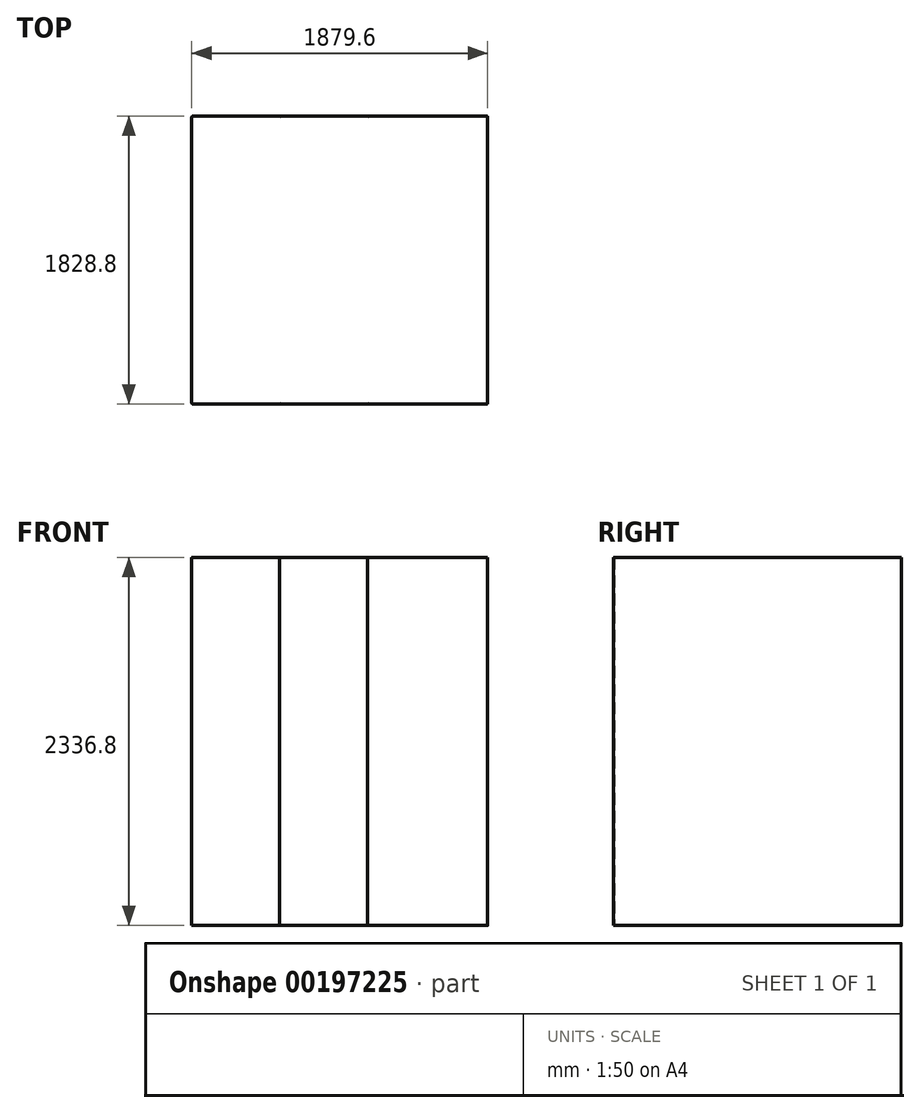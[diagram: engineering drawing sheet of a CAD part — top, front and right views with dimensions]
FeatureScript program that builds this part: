
annotation { "Feature Type Name" : "Feature", "Feature Type Description" : "" }
export const myFeature = defineFeature(function(context is Context, id is Id, definition is map)
    precondition{}
    {
        {
            var Q0;
            Q0=qCreatedBy(makeId("Top.planeOp"),FACE);
            var sketch = newSketch(context, id + "F0", { "sketchPlane" : qUnion([Q0])});
            skLineSegment(sketch, "E0.bottom", {"start": v(-285.75, 914.4) * mm, "end": v(-831.85, 914.4) * mm});
            skLineSegment(sketch, "E0.top", {"start": v(-285.75, -914.4) * mm, "end": v(-831.85, -914.4) * mm});
            skLineSegment(sketch, "E0.left", {"start": v(-279.4, 908.05) * mm, "end": v(-279.4, -908.05) * mm});
            skLineSegment(sketch, "E0.right", {"start": v(-838.2, 908.05) * mm, "end": v(-838.2, -908.05) * mm});
            skPoint(sketch, "E0.middle", {"position": v(-558.8, 0) * mm});
            skLineSegment(sketch, "E1.bottom", {"start": v(273.05, 914.4) * mm, "end": v(-273.05, 914.4) * mm});
            skLineSegment(sketch, "E1.top", {"start": v(273.05, -914.4) * mm, "end": v(-273.05, -914.4) * mm});
            skLineSegment(sketch, "E1.left", {"start": v(279.4, 908.05) * mm, "end": v(279.4, -908.05) * mm});
            skPoint(sketch, "E1.middle", {"position": v(0, 0) * mm});
            skLineSegment(sketch, "E2.bottom", {"start": v(1035.05, 914.4) * mm, "end": v(285.75, 914.4) * mm});
            skLineSegment(sketch, "E2.top", {"start": v(1035.05, -914.4) * mm, "end": v(285.75, -914.4) * mm});
            skLineSegment(sketch, "E2.left", {"start": v(1041.4, 908.05) * mm, "end": v(1041.4, -908.05) * mm});
            skPoint(sketch, "E2.middle", {"position": v(660.4, 0) * mm});
            skPoint(sketch, "E3.visualSharp", {"position": v(279.4, -914.4) * mm});
            skArc(sketch, "E3.filletArc", {"start": v(279.4, -908.05) * mm, "mid": v(281.26, -912.54) * mm, "end": v(285.75, -914.4) * mm});
            skArc(sketch, "E4.filletArc", {"start": v(273.05, -914.4) * mm, "mid": v(277.54, -912.54) * mm, "end": v(279.4, -908.05) * mm});
            skPoint(sketch, "E5.visualSharp", {"position": v(1041.4, -914.4) * mm});
            skArc(sketch, "E5.filletArc", {"start": v(1035.05, -914.4) * mm, "mid": v(1039.54, -912.54) * mm, "end": v(1041.4, -908.05) * mm});
            skPoint(sketch, "E6.visualSharp", {"position": v(1041.4, 914.4) * mm});
            skArc(sketch, "E6.filletArc", {"start": v(1041.4, 908.05) * mm, "mid": v(1039.54, 912.54) * mm, "end": v(1035.05, 914.4) * mm});
            skPoint(sketch, "E7.visualSharp", {"position": v(279.4, 914.4) * mm});
            skArc(sketch, "E7.filletArc", {"start": v(285.75, 914.4) * mm, "mid": v(281.26, 912.54) * mm, "end": v(279.4, 908.05) * mm});
            skArc(sketch, "E8.filletArc", {"start": v(279.4, 908.05) * mm, "mid": v(277.54, 912.54) * mm, "end": v(273.05, 914.4) * mm});
            skPoint(sketch, "E9.visualSharp", {"position": v(-279.4, 914.4) * mm});
            skArc(sketch, "E9.filletArc", {"start": v(-279.4, 908.05) * mm, "mid": v(-281.26, 912.54) * mm, "end": v(-285.75, 914.4) * mm});
            skArc(sketch, "E10.filletArc", {"start": v(-273.05, 914.4) * mm, "mid": v(-277.54, 912.54) * mm, "end": v(-279.4, 908.05) * mm});
            skPoint(sketch, "E11.visualSharp", {"position": v(-838.2, 914.4) * mm});
            skArc(sketch, "E11.filletArc", {"start": v(-831.85, 914.4) * mm, "mid": v(-836.34, 912.54) * mm, "end": v(-838.2, 908.05) * mm});
            skPoint(sketch, "E12.visualSharp", {"position": v(-838.2, -914.4) * mm});
            skArc(sketch, "E12.filletArc", {"start": v(-838.2, -908.05) * mm, "mid": v(-836.34, -912.54) * mm, "end": v(-831.85, -914.4) * mm});
            skPoint(sketch, "E13.visualSharp", {"position": v(-279.4, -914.4) * mm});
            skArc(sketch, "E13.filletArc", {"start": v(-285.75, -914.4) * mm, "mid": v(-281.26, -912.54) * mm, "end": v(-279.4, -908.05) * mm});
            skArc(sketch, "E14.filletArc", {"start": v(-279.4, -908.05) * mm, "mid": v(-277.54, -912.54) * mm, "end": v(-273.05, -914.4) * mm});
            skSolve(sketch);
        }
        {
            var Q0;
            Q0=makeQuery(id+"F0.imprint","IMPRINT",FACE,{"disambiguationData":[TD([[makeQuery(id+"F0.imprint","IMPRINT",EDGE,{"derivedFrom":sQuery(id+"F0.wireOp",EDGE,"E0.bottom")}),1.0]])]});
            var Q1;
            Q1=makeQuery(id+"F0.imprint","IMPRINT",FACE,{"disambiguationData":[TD([[makeQuery(id+"F0.imprint","IMPRINT",EDGE,{"derivedFrom":sQuery(id+"F0.wireOp",EDGE,"E1.bottom")}),1.0]])]});
            var Q2;
            Q2=makeQuery(id+"F0.imprint","IMPRINT",FACE,{"disambiguationData":[TD([[makeQuery(id+"F0.imprint","IMPRINT",EDGE,{"derivedFrom":sQuery(id+"F0.wireOp",EDGE,"E2.bottom")}),1.0]])]});
            extrude(context, id + "F1", {"entities" : qUnion([Q0, Q1, Q2]), "depth" : 2336.8 * mm});
        }
    });
